# Revit family: Electronics_Medium-Large-Room-Solutions_Biamp_Devio_Conference-Room-Hub_SCX__
name_source: partatom
category: Communication Devices
units: mm (PartAtom-declared; Revit-internal decimal feet)

## family parameters
Cut with Voids When Loaded = Yes
Host = Face
Maintain Annotation Orientation = No
OmniClass Number = 23.85.10.14
OmniClass Title = Visual Information Systems
Part Type = Normal
Room Calculation Point = No
Round Connector Dimension = Use Diameter
Shared = No

## types (2) — shared parameters
Altitude = 0-6,600 ft (0-2000m) MSL
Apparent Load = 150 VA
Bit Depth = 16-bit / 24-bit
Compliance = FCC Part 15B (USA); Canada ICES-003 (A) / NMB-003 (A); CE marked (Europe); UL und C-UL listed (USA and Canada); RCM (Australia); RoHS Directive (Europe)
Connector Description = 100 - 240V 50/60Hz
Default Elevation = 48 "
Depth = 8.1 "
Height = 1.5 "
Housing Material = Biamp - Metal - Dark Gray
Humidity = 0-98% relative humidity (non-condensing)
Manufacturer = Biamp
Max Power Consumption = 150 W
No Mount = No mount
Number of Channels = up to 2x2
Number of Poles = 1
Power Factor = 1
Product Documentation Link = https://downloads.biamp.com
Product Page URL = https://www.biamp.com
Product data url = https://www.bimobject.com
Sampling Rate = 48kHz
Temperature Range = 32 - 104° F (0 - 40° C)
URL = https://www.biamp.com
Voltage = 120 V
Weight = 1.90 lbf
Width = 8.1 "
_Plenum Box 12x12 = Plenum Box 12x12
_RMX 100 Rack Shelf = RMX 100 Rack Shelf

## per-type parameters (varying)
| type | Description | Model |
| SCX 400 | Devio® SCX 400 Conference Room Hub | Devio SCX 400 |
| SCX 800 | Devio® SCX 800 Conference Room Hub | Devio SCX 800 |

## geometry (parser evidence)
native form markers: Sweep x13
no freeform markers — native parametric forms only
